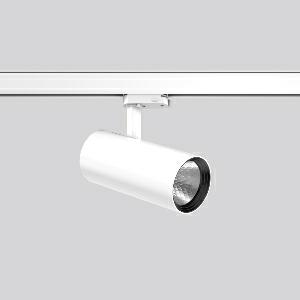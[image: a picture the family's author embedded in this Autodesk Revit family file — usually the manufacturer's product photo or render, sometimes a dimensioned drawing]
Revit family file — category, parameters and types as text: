
# Revit family: deecos_s_mini_742203_002_2_76_31fa
name_source: partatom
category: Lighting Fixtures
units: mm (PartAtom-declared; Revit-internal decimal feet)

## family parameters
Cut with Voids When Loaded = No
Host = Face
Light Source = No
Part Type = Normal
Room Calculation Point = No
Round Connector Dimension = Use Diameter
Shared = No

## types (1)
- DEECOS S mini (1 x LED Modul 927, 3400 lm, 2700)
    Apparent Load = 29 VA
    Approval mark = CE
    CIE Flux Codes = 100 100 100 100 100
    Color Rendering = 92
    Color Temperature = 2700
    Default Elevation = 1800 mm
    Description = Series: DEECOS S mini
LED surface-mounted projector in modern design with no visible cooling ribs. Housing: die-cast aluminium, powder-coated. Rotation range: 356°. Swivel range: 90°. Black plastic ring and recessed LED to prevent glare from the side. Optical assembly with reflector made of MIRO-Silver with 98% total light reflection for outstanding efficiency - can be changed without tools. Best colour rendering index Ra>90. With adapter for RZB 3-circuit DALI tracks. Suitable for Track on ceiling, Wall track. High quality converter without flickering and stroboscopic effect. The following accessories can be mounted without use of tools: interchangeable lenses, decorative glasses, honeycomb louvre, clear and frosted diffusers, white interchangeable plastic ring. 
Colour: traffic white, matt (RAL 9016)
Diameter: 87 mm
Height: 214 mm
Lamp: LED
Socket: without socket
Colour temperature: 2700K
Colour rendering index (CRI): 92
System power: 29 W
Rated luminous flux: 3400 lm
Luminous efficiency: 117 lm/W
Control gear: Converter, dimmable, DALI
Protection class: I
Type of protection: IP 20
    Height = 214 mm
    Lamp = 1 x LED Modul 927
    Lamp Light Flux = 3400 lm
    Lamp count = 1
    Length = 87 mm
    Lifetime = 50000 h
    Luminous efficacy = 117 lm/W
    Manufacturer = RZB
    ModVariant = No
    Model = 742203.002.2.76
    Mounting Place = Ceiling
    Mounting Type = Rail mounted
    Number of Poles = 1
    OnlyDefault = Yes
    Power Factor = 1
    Product Name = DEECOS S mini
    Product group = Track mounted projectors
    ProductGroupID = 301
    Protection Class = Protection class I
    Protection Degree = IP 20
    RLX_Detail_Level = 1
    RLX_Emergency_Light_Flux = 0 lm
    RLX_Emergency_Type = 0
    RLX_Emergency_Type_DB = No
    RlxData = <blob elided: 35021 chars, md5=12c99ccf>
    Socket = socket
    Standby Power = 0 W
    System Light Flux = 3400 lm
    System Power = 29 W
    Type Comments = Product without accessories
    Type Image = 741926.002.jpg
    URL = http://relux.com
    VarID = ---
    Voltage = 230 V
    Voltage Range = 220-240 V
    Weight = 0.00 kg
    Width = 0 mm  [stored 0 ft]

note: [stored X ft] marks values corroborated as IEEE doubles in the binary element streams (Revit-internal decimal feet)

## geometry (parser evidence)
native form markers: Blend x4, Sweep x11
no freeform markers — native parametric forms only
